# Revit family: PDI
name_source: partatom
category: Air Terminals
revit_build: Autodesk Revit MEP 2012 (Build: 20110309_2315(x64)
units: mm (PartAtom-declared; Revit-internal decimal feet)

## types (43) — shared parameters
Alto base = 5/8"
Alto plato = 2 1/2"
Manufacturer = INNES
Material = Aluminio/Fierro/Inox
URL = http://www.innes.com.mx

## per-type parameters (varying)
| type | A cuello | B plato | Base 1 | Base 2 | Cuello | Cuello Cuadrado | Cuello Redondo | Diametro interior | Max Flow | Min Flow | Máxima presión estática | Máxima velocidad de cuello | Máximo nivel de ruido (NC) | Mínima presión estática | Mínima velocidad de cuello | Radio |
| PDI-C-06-12 | 5 7/8" | 11 3/4" | 11" | 10 3/8" | Cuadrado | Yes | No | 2 13/16" | 250 CFM | 50 CFM | 0.10 in-wg | 1275 FPM | 40 | 0.02 in-wg | 255 FPM | 2 15/16" |
| PDI-C-08-12 | 7 7/8" | 11 3/4" | 11" | 10 3/8" | Cuadrado | Yes | No | 3 13/16" | 0 CFM | 0 CFM | 0.00 in-wg | 0 FPM | 0 | 0.00 in-wg | 0 FPM | 3 15/16" |
| PDI-C-10-12 | 9 7/8" | 11 3/4" | 11" | 10 3/8" | Cuadrado | Yes | No | 4 13/16" | 0 CFM | 0 CFM | 0.00 in-wg | 0 FPM | 0 | 0.00 in-wg | 0 FPM | 4 15/16" |
| PDI-R-06-12 | 5 7/8" | 11 3/4" | 11" | 10 3/8" | Redondo | No | Yes | 2 13/16" | 250 CFM | 50 CFM | 0.10 in-wg | 1275 FPM | 40 | 0.02 in-wg | 255 FPM | 2 15/16" |
| PDI-R-08-12 | 7 7/8" | 11 3/4" | 11" | 10 3/8" | Redondo | No | Yes | 3 13/16" | 0 CFM | 0 CFM | 0.00 in-wg | 0 FPM | 0 | 0.00 in-wg | 0 FPM | 3 15/16" |
| PDI-C-06-16 | 5 7/8" | 15 3/4" | 15" | 14" | Cuadrado | Yes | No | 2 13/16" | 0 CFM | 0 CFM | 0.00 in-wg | 0 FPM | 0 | 0.00 in-wg | 0 FPM | 2 15/16" |
| PDI-C-08-16 | 7 7/8" | 15 3/4" | 15" | 14" | Cuadrado | Yes | No | 3 13/16" | 500 CFM | 100 CFM | 0.13 in-wg | 1430 FPM | 46 | 0.01 in-wg | 285 FPM | 3 15/16" |
| PDI-C-10-16 | 9 7/8" | 15 3/4" | 15" | 14" | Cuadrado | Yes | No | 4 13/16" | 0 CFM | 0 CFM | 0.00 in-wg | 0 FPM | 0 | 0.00 in-wg | 0 FPM | 4 15/16" |
| PDI-C-12-16 | 11 7/8" | 15 3/4" | 15" | 14" | Cuadrado | Yes | No | 5 13/16" | 0 CFM | 0 CFM | 0.00 in-wg | 0 FPM | 0 | 0.00 in-wg | 0 FPM | 5 15/16" |
| PDI-C-14-16 | 13 7/8" | 15 3/4" | 15" | 14" | Cuadrado | Yes | No | 6 13/16" | 0 CFM | 0 CFM | 0.00 in-wg | 0 FPM | 0 | 0.00 in-wg | 0 FPM | 6 15/16" |
| PDI-R-06-16 | 5 7/8" | 15 3/4" | 15" | 14" | Redondo | No | Yes | 2 13/16" | 0 CFM | 0 CFM | 0.00 in-wg | 0 FPM | 0 | 0.00 in-wg | 0 FPM | 2 15/16" |
| PDI-R-08-16 | 7 7/8" | 15 3/4" | 15" | 14" | Redondo | No | Yes | 3 13/16" | 500 CFM | 100 CFM | 0.13 in-wg | 1430 FPM | 46 | 0.01 in-wg | 285 FPM | 3 15/16" |
| PDI-R-10-16 | 9 7/8" | 15 3/4" | 15" | 14" | Redondo | No | Yes | 4 13/16" | 0 CFM | 0 CFM | 0.00 in-wg | 0 FPM | 0 | 0.00 in-wg | 0 FPM | 4 15/16" |
| PDI-R-12-16 | 11 7/8" | 15 3/4" | 15" | 14" | Redondo | No | Yes | 5 13/16" | 0 CFM | 0 CFM | 0.00 in-wg | 0 FPM | 0 | 0.00 in-wg | 0 FPM | 5 15/16" |
| PDI-C-06-20 | 5 7/8" | 19 3/4" | 19" | 18" | Cuadrado | Yes | No | 2 13/16" | 0 CFM | 0 CFM | 0.00 in-wg | 0 FPM | 0 | 0.00 in-wg | 0 FPM | 2 15/16" |
| PDI-C-08-20 | 7 7/8" | 19 3/4" | 19" | 18" | Cuadrado | Yes | No | 3 13/16" | 0 CFM | 0 CFM | 0.00 in-wg | 0 FPM | 0 | 0.00 in-wg | 0 FPM | 3 15/16" |
| PDI-C-10-20 | 9 7/8" | 19 3/4" | 19" | 18" | Cuadrado | Yes | No | 4 13/16" | 800 CFM | 150 CFM | 0.17 in-wg | 1380 FPM | 44 | 0.01 in-wg | 275 FPM | 4 15/16" |
| PDI-C-12-20 | 11 7/8" | 19 3/4" | 19" | 18" | Cuadrado | Yes | No | 5 13/16" | 0 CFM | 0 CFM | 0.00 in-wg | 0 FPM | 0 | 0.00 in-wg | 0 FPM | 5 15/16" |
| PDI-C-14-20 | 13 7/8" | 19 3/4" | 19" | 18" | Cuadrado | Yes | No | 6 13/16" | 0 CFM | 0 CFM | 0.00 in-wg | 0 FPM | 0 | 0.00 in-wg | 0 FPM | 6 15/16" |
| PDI-C-16-20 | 15 7/8" | 19 3/4" | 19" | 18" | Cuadrado | Yes | No | 7 13/16" | 0 CFM | 0 CFM | 0.00 in-wg | 0 FPM | 0 | 0.00 in-wg | 0 FPM | 7 15/16" |
| PDI-C-18-20 | 17 7/8" | 19 3/4" | 19" | 18" | Cuadrado | Yes | No | 8 13/16" | 0 CFM | 0 CFM | 0.00 in-wg | 0 FPM | 0 | 0.00 in-wg | 0 FPM | 8 15/16" |
| PDI-R-06-20 | 5 7/8" | 19 3/4" | 19" | 18" | Redondo | No | Yes | 2 13/16" | 0 CFM | 0 CFM | 0.00 in-wg | 0 FPM | 0 | 0.00 in-wg | 0 FPM | 2 15/16" |
| PDI-R-08-20 | 7 7/8" | 19 3/4" | 19" | 18" | Redondo | No | Yes | 3 13/16" | 0 CFM | 0 CFM | 0.00 in-wg | 0 FPM | 0 | 0.00 in-wg | 0 FPM | 3 15/16" |
| PDI-R-10-20 | 9 7/8" | 19 3/4" | 19" | 18" | Redondo | No | Yes | 4 13/16" | 800 CFM | 150 CFM | 0.17 in-wg | 1380 FPM | 44 | 0.01 in-wg | 275 FPM | 4 15/16" |
| PDI-R-12-20 | 11 7/8" | 19 3/4" | 19" | 18" | Redondo | No | Yes | 5 13/16" | 0 CFM | 0 CFM | 0.00 in-wg | 0 FPM | 0 | 0.00 in-wg | 0 FPM | 5 15/16" |
| PDI-R-14-20 | 13 7/8" | 19 3/4" | 19" | 18" | Redondo | No | Yes | 6 13/16" | 0 CFM | 0 CFM | 0.00 in-wg | 0 FPM | 0 | 0.00 in-wg | 0 FPM | 6 15/16" |
| PDI-R-16-20 | 15 7/8" | 19 3/4" | 19" | 18" | Redondo | No | Yes | 7 13/16" | 0 CFM | 0 CFM | 0.00 in-wg | 0 FPM | 0 | 0.00 in-wg | 0 FPM | 7 15/16" |
| PDI-C-06-24 | 5 7/8" | 23 3/4" | 23" | 22" | Cuadrado | Yes | No | 2 13/16" | 300 CFM | 50 CFM | 0.08 in-wg | 1530 FPM | 44 | 0.01 in-wg | 255 FPM | 2 15/16" |
| PDI-C-08-24 | 7 7/8" | 23 3/4" | 23" | 22" | Cuadrado | Yes | No | 3 13/16" | 600 CFM | 100 CFM | 0.12 in-wg | 1430 FPM | 44 | 0.01 in-wg | 285 FPM | 3 15/16" |
| PDI-C-10-24 | 9 7/8" | 23 3/4" | 23" | 22" | Cuadrado | Yes | No | 4 13/16" | 800 CFM | 150 CFM | 0.20 in-wg | 1470 FPM | 46 | 0.01 in-wg | 275 FPM | 4 15/16" |
| PDI-C-12-24 | 11 7/8" | 23 3/4" | 23" | 22" | Cuadrado | Yes | No | 5 13/16" | 900 CFM | 200 CFM | 0.15 in-wg | 1150 FPM | 44 | 0.01 in-wg | 255 FPM | 5 15/16" |
| PDI-C-14-24 | 13 7/8" | 23 3/4" | 23" | 22" | Cuadrado | Yes | No | 6 13/16" | 1500 CFM | 350 CFM | 0.26 in-wg | 1400 FPM | 53 | 0.01 in-wg | 330 FPM | 6 15/16" |
| PDI-C-16-24 | 15 7/8" | 23 3/4" | 23" | 22" | Cuadrado | Yes | No | 7 13/16" | 1800 CFM | 600 CFM | 0.22 in-wg | 1160 FPM | 51 | 0.03 in-wg | 430 FPM | 7 15/16" |
| PDI-C-18-24 | 17 7/8" | 23 3/4" | 23" | 22" | Cuadrado | Yes | No | 8 13/16" | 0 CFM | 0 CFM | 0.00 in-wg | 0 FPM | 0 | 0.00 in-wg | 0 FPM | 8 15/16" |
| PDI-C-20-24 | 19 7/8" | 23 3/4" | 23" | 22" | Cuadrado | Yes | No | 9 13/16" | 0 CFM | 0 CFM | 0.00 in-wg | 0 FPM | 0 | 0.00 in-wg | 0 FPM | 9 15/16" |
| PDI-C-22-24 | 21 7/8" | 23 3/4" | 23" | 22" | Cuadrado | Yes | No | 10 13/16" | 0 CFM | 0 CFM | 0.00 in-wg | 0 FPM | 0 | 0.00 in-wg | 0 FPM | 10 15/16" |
| PDI-R-06-24 | 5 7/8" | 23 3/4" | 23" | 22" | Redondo | No | Yes | 2 13/16" | 300 CFM | 50 CFM | 0.08 in-wg | 1530 FPM | 44 | 0.01 in-wg | 255 FPM | 2 15/16" |
| PDI-R-08-24 | 7 7/8" | 23 3/4" | 23" | 22" | Redondo | No | Yes | 3 13/16" | 600 CFM | 100 CFM | 0.12 in-wg | 1430 FPM | 44 | 0.01 in-wg | 285 FPM | 3 15/16" |
| PDI-R-10-24 | 9 7/8" | 23 3/4" | 23" | 22" | Redondo | No | Yes | 4 13/16" | 800 CFM | 150 CFM | 0.20 in-wg | 1470 FPM | 46 | 0.01 in-wg | 275 FPM | 4 15/16" |
| PDI-R-12-24 | 11 7/8" | 23 3/4" | 23" | 22" | Redondo | No | Yes | 5 13/16" | 900 CFM | 200 CFM | 0.15 in-wg | 1150 FPM | 44 | 0.01 in-wg | 255 FPM | 5 15/16" |
| PDI-R-14-24 | 13 7/8" | 23 3/4" | 23" | 22" | Redondo | No | Yes | 6 13/16" | 1500 CFM | 350 CFM | 0.26 in-wg | 1400 FPM | 53 | 0.01 in-wg | 330 FPM | 6 15/16" |
| PDI-R-16-24 | 15 7/8" | 23 3/4" | 23" | 22" | Redondo | No | Yes | 7 13/16" | 1800 CFM | 600 CFM | 0.22 in-wg | 1160 FPM | 51 | 0.03 in-wg | 430 FPM | 7 15/16" |
| PDI-R-18-24 | 17 7/8" | 23 3/4" | 23" | 22" | Redondo | No | Yes | 8 13/16" | 0 CFM | 0 CFM | 0.00 in-wg | 0 FPM | 0 | 0.00 in-wg | 0 FPM | 8 15/16" |

## geometry (parser evidence)
native form markers: Blend x6, Sweep x1
no freeform markers — native parametric forms only
